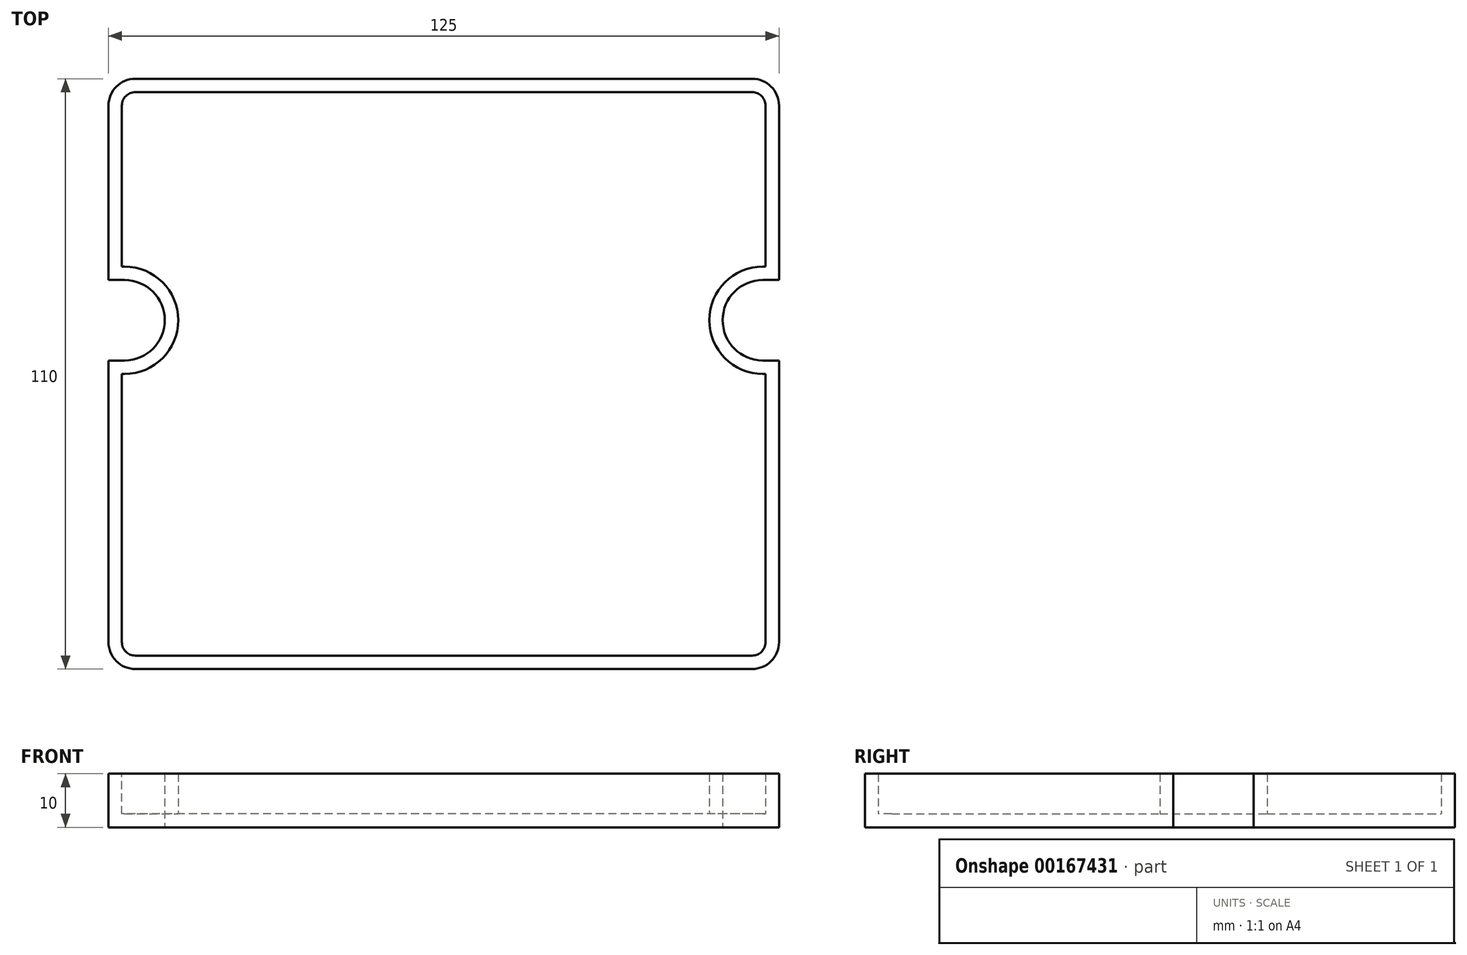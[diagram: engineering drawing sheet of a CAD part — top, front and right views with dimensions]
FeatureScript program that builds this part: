
annotation { "Feature Type Name" : "Feature", "Feature Type Description" : "" }
export const myFeature = defineFeature(function(context is Context, id is Id, definition is map)
    precondition{}
    {
        {
            var Q0;
            Q0=qCreatedBy(makeId("Top.planeOp"),FACE);
            var sketch = newSketch(context, id + "F0", { "sketchPlane" : qUnion([Q0])});
            skLineSegment(sketch, "E0.bottom", {"start": v(57.5, -55) * mm, "end": v(-57.5, -55) * mm});
            skLineSegment(sketch, "E0.top", {"start": v(57.5, 55) * mm, "end": v(-57.5, 55) * mm});
            skLineSegment(sketch, "E0.left", {"start": v(62.5, -50) * mm, "end": v(62.5, 2.5) * mm});
            skLineSegment(sketch, "E0.right", {"start": v(-62.5, -50) * mm, "end": v(-62.5, 2.5) * mm});
            skPoint(sketch, "E0.middle", {"position": v(0, 0) * mm});
            skArc(sketch, "E1", {"start": v(-59.5, 2.5) * mm, "mid": v(-52, 10) * mm, "end": v(-59.5, 17.5) * mm});
            skLineSegment(sketch, "E2", {"start": v(-59.5, 2.5) * mm, "end": v(-62.5, 2.5) * mm});
            skLineSegment(sketch, "E3", {"start": v(-59.5, 17.5) * mm, "end": v(-62.5, 17.5) * mm});
            skLineSegment(sketch, "E4.trimOffspring", {"start": v(-62.5, 17.5) * mm, "end": v(-62.5, 50) * mm});
            skLineSegment(sketch, "E5.MirrorCS", {"start": v(59.5, 17.5) * mm, "end": v(62.5, 17.5) * mm});
            skLineSegment(sketch, "E6.MirrorCS", {"start": v(59.5, 2.5) * mm, "end": v(62.5, 2.5) * mm});
            skArc(sketch, "E7.MirrorCS", {"start": v(59.5, 2.5) * mm, "mid": v(52, 10) * mm, "end": v(59.5, 17.5) * mm});
            skLineSegment(sketch, "E8.trimOffspring", {"start": v(62.5, 17.5) * mm, "end": v(62.5, 50) * mm});
            skPoint(sketch, "E9.visualSharp", {"position": v(-62.5, 55) * mm});
            skArc(sketch, "E9.filletArc", {"start": v(-57.5, 55) * mm, "mid": v(-61.04, 53.54) * mm, "end": v(-62.5, 50) * mm});
            skPoint(sketch, "E10.visualSharp", {"position": v(62.5, 55) * mm});
            skArc(sketch, "E10.filletArc", {"start": v(62.5, 50) * mm, "mid": v(61.04, 53.54) * mm, "end": v(57.5, 55) * mm});
            skPoint(sketch, "E11.visualSharp", {"position": v(62.5, -55) * mm});
            skArc(sketch, "E11.filletArc", {"start": v(57.5, -55) * mm, "mid": v(61.04, -53.54) * mm, "end": v(62.5, -50) * mm});
            skPoint(sketch, "E12.visualSharp", {"position": v(-62.5, -55) * mm});
            skArc(sketch, "E12.filletArc", {"start": v(-62.5, -50) * mm, "mid": v(-61.04, -53.54) * mm, "end": v(-57.5, -55) * mm});
            skSolve(sketch);
        }
        {
            var Q0;
            Q0=makeQuery(id+"F0.imprint","IMPRINT",FACE,{"disambiguationData":[TD([[makeQuery(id+"F0.imprint","IMPRINT",EDGE,{"derivedFrom":sQuery(id+"F0.wireOp",EDGE,"E0.bottom")}),-1.0]])]});
            extrude(context, id + "F1", {"entities" : qUnion([Q0]), "depth" : 10 * mm});
        }
        {
            var Q0;
            Q0=makeQuery(id+"F1.opExtrude","CAP_FACE",FACE,{"disambiguationData":[OSD([sQuery(id+"F0.wireOp",EDGE,"E0.bottom"),sQuery(id+"F0.wireOp",EDGE,"E0.top"),sQuery(id+"F0.wireOp",EDGE,"E0.left"),sQuery(id+"F0.wireOp",EDGE,"E0.right"),sQuery(id+"F0.wireOp",EDGE,"E1"),sQuery(id+"F0.wireOp",EDGE,"E2"),sQuery(id+"F0.wireOp",EDGE,"E3"),sQuery(id+"F0.wireOp",EDGE,"E4.trimOffspring"),sQuery(id+"F0.wireOp",EDGE,"E5.MirrorCS"),sQuery(id+"F0.wireOp",EDGE,"E6.MirrorCS"),sQuery(id+"F0.wireOp",EDGE,"E7.MirrorCS"),sQuery(id+"F0.wireOp",EDGE,"E8.trimOffspring"),sQuery(id+"F0.wireOp",EDGE,"E9.filletArc"),sQuery(id+"F0.wireOp",EDGE,"E10.filletArc"),sQuery(id+"F0.wireOp",EDGE,"E11.filletArc"),sQuery(id+"F0.wireOp",EDGE,"E12.filletArc")])],"isStart":false});
            shell(context, id + "F2", {"entities" : qUnion([Q0]), "thickness" : 2.5 * mm});
        }
    });
